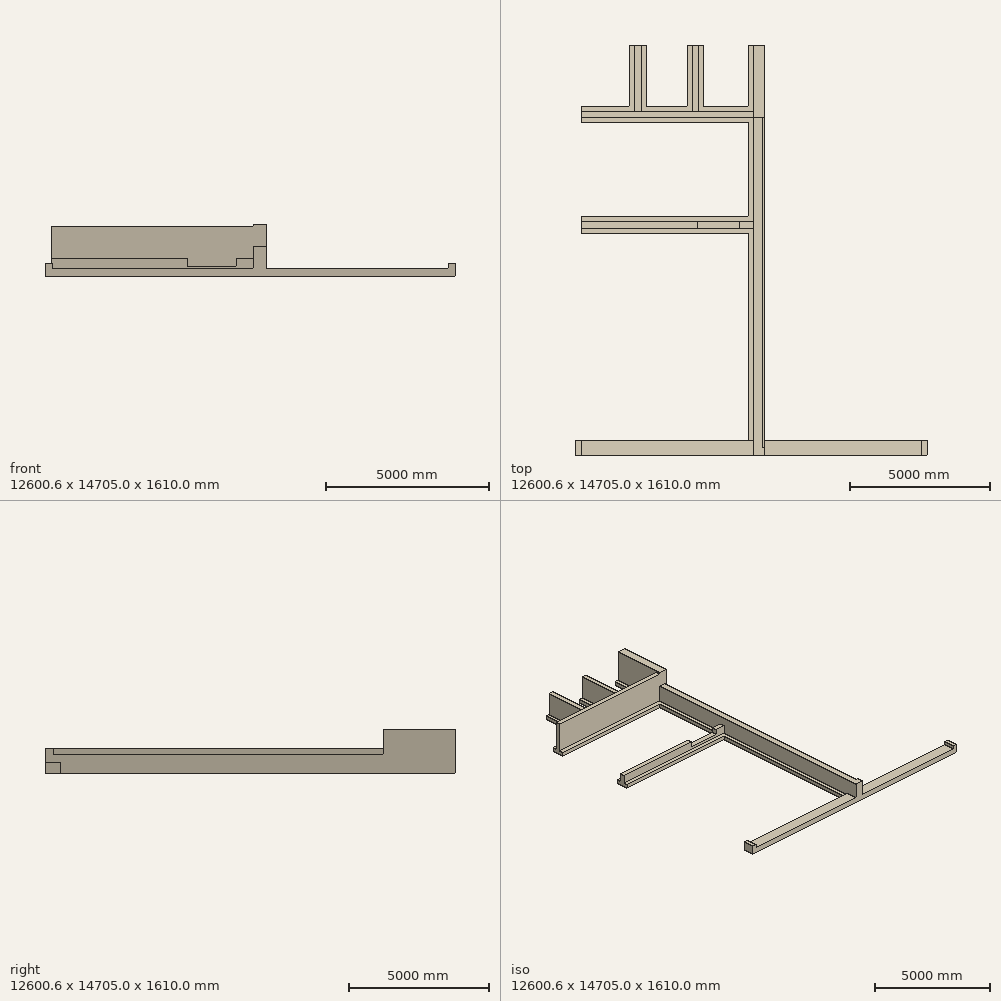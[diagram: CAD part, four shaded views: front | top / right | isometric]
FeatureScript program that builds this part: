
annotation { "Feature Type Name" : "Feature", "Feature Type Description" : "" }
export const myFeature = defineFeature(function(context is Context, id is Id, definition is map)
    precondition{}
    {
        {
            var Q0;
            Q0=qCreatedBy(makeId("Top.planeOp"),FACE);
            var sketch = newSketch(context, id + "F0", { "sketchPlane" : qUnion([Q0])});
            skLineSegment(sketch, "E0.bottom", {"start": v(0, 0) * mm, "end": v(590, 0) * mm});
            skLineSegment(sketch, "E0.top", {"start": v(0, 14705) * mm, "end": v(590, 14705) * mm});
            skLineSegment(sketch, "E0.left", {"start": v(0, 0) * mm, "end": v(0, 14705) * mm});
            skLineSegment(sketch, "E0.right", {"start": v(590, 0) * mm, "end": v(590, 14705) * mm});
            skLineSegment(sketch, "E1.bottom", {"start": v(0, 11945) * mm, "end": v(-5990, 11945) * mm});
            skLineSegment(sketch, "E1.top", {"start": v(0, 12535) * mm, "end": v(-5990, 12535) * mm});
            skLineSegment(sketch, "E1.right", {"start": v(-5990, 11945) * mm, "end": v(-5990, 12535) * mm});
            skLineSegment(sketch, "E2.bottom", {"start": v(0, 7965) * mm, "end": v(-5990, 7965) * mm});
            skLineSegment(sketch, "E2.top", {"start": v(0, 8555) * mm, "end": v(-5990, 8555) * mm});
            skLineSegment(sketch, "E2.right", {"start": v(-5990, 7965) * mm, "end": v(-5990, 8555) * mm});
            skLineSegment(sketch, "E3.bottom", {"start": v(-4250, 14705) * mm, "end": v(-3660, 14705) * mm});
            skLineSegment(sketch, "E3.left", {"start": v(-4250, 14705) * mm, "end": v(-4250, 12535) * mm});
            skLineSegment(sketch, "E3.right", {"start": v(-3660, 14705) * mm, "end": v(-3660, 12535) * mm});
            skLineSegment(sketch, "E4.top", {"start": v(-2200, 14705) * mm, "end": v(-1610, 14705) * mm});
            skLineSegment(sketch, "E4.left", {"start": v(-2200, 12535) * mm, "end": v(-2200, 14705) * mm});
            skLineSegment(sketch, "E4.right", {"start": v(-1610, 12535) * mm, "end": v(-1610, 14705) * mm});
            skSolve(sketch);
        }
        {
            var Q0;
            {var subQ3=sQuery(id+"F0.wireOp",EDGE,"E0.bottom");Q0=makeQuery(id+"F0.imprint","IMPRINT",FACE,{"disambiguationData":[TD([[makeQuery(id+"F0.imprint","IMPRINT",EDGE,{"derivedFrom":subQ3}),1.0]])]});}
            var Q1;
            Q1=makeQuery(id+"F0.imprint","IMPRINT",FACE,{"disambiguationData":[TD([[makeQuery(id+"F0.imprint","IMPRINT",EDGE,{"derivedFrom":sQuery(id+"F0.wireOp",EDGE,"E2.bottom")}),-1.0]])]});
            var Q2;
            Q2=makeQuery(id+"F0.imprint","IMPRINT",FACE,{"disambiguationData":[TD([[makeQuery(id+"F0.imprint","IMPRINT",EDGE,{"derivedFrom":sQuery(id+"F0.wireOp",EDGE,"E1.bottom")}),-1.0]])]});
            var Q3;
            Q3=makeQuery(id+"F0.imprint","IMPRINT",FACE,{"disambiguationData":[TD([[makeQuery(id+"F0.imprint","IMPRINT",EDGE,{"derivedFrom":sQuery(id+"F0.wireOp",EDGE,"E3.bottom")}),-1.0]])]});
            var Q4;
            Q4=makeQuery(id+"F0.imprint","IMPRINT",FACE,{"disambiguationData":[TD([[makeQuery(id+"F0.imprint","IMPRINT",EDGE,{"derivedFrom":sQuery(id+"F0.wireOp",EDGE,"yrg7KJtE-bSgN-jth9-biQU-cp0C4ELDEyeg.bottom")}),1.0]])]});
            var Q5;
            Q5=makeQuery(id+"F0.imprint","IMPRINT",FACE,{"disambiguationData":[TD([[makeQuery(id+"F0.imprint","IMPRINT",EDGE,{"derivedFrom":sQuery(id+"F0.wireOp",EDGE,"E4.top")}),-1.0]])]});
            extrude(context, id + "F1", {"entities" : qUnion([Q0, Q1, Q2, Q3, Q4, Q5]), "depth" : 180 * mm});
        }
        {
            var Q0;
            Q0=makeQuery(id+"F1.opExtrude","CAP_FACE",FACE,{"disambiguationData":[OSD([sQuery(id+"F0.wireOp",EDGE,"E0.bottom"),sQuery(id+"F0.wireOp",EDGE,"E0.top"),sQuery(id+"F0.wireOp",EDGE,"E0.left"),sQuery(id+"F0.wireOp",EDGE,"E0.right"),sQuery(id+"F0.wireOp",EDGE,"E1.bottom"),sQuery(id+"F0.wireOp",EDGE,"E1.top"),sQuery(id+"F0.wireOp",EDGE,"E1.right"),sQuery(id+"F0.wireOp",EDGE,"E2.bottom"),sQuery(id+"F0.wireOp",EDGE,"E2.top"),sQuery(id+"F0.wireOp",EDGE,"E2.right"),sQuery(id+"F0.wireOp",EDGE,"E3.bottom"),sQuery(id+"F0.wireOp",EDGE,"E3.left"),sQuery(id+"F0.wireOp",EDGE,"E3.right")])],"isStart":false});
            var sketch = newSketch(context, id + "F2", { "sketchPlane" : qUnion([Q0])});
            skLineSegment(sketch, "E5.bottom", {"start": v(590, 0) * mm, "end": v(195, 0) * mm});
            skLineSegment(sketch, "E5.top", {"start": v(590, 14705) * mm, "end": v(195, 14705) * mm});
            skLineSegment(sketch, "E5.left", {"start": v(590, 0) * mm, "end": v(590, 14705) * mm});
            skLineSegment(sketch, "E5.right", {"start": v(195, 0) * mm, "end": v(195, 14705) * mm});
            skSolve(sketch);
        }
        {
            var Q0;
            Q0 = qSketchRegion(id + "F2", true);
            extrude(context, id + "F3", {"entities" : qUnion([Q0]), "operationType" : NewBodyOperationType.ADD, "depth" : 750 * mm});
        }
        {
            var Q0;
            Q0=makeQuery(id+"F3.opExtrude","CAP_FACE",FACE,{"disambiguationData":[OSD([sQuery(id+"F2.wireOp",EDGE,"E5.bottom"),sQuery(id+"F2.wireOp",EDGE,"E5.top"),sQuery(id+"F2.wireOp",EDGE,"E5.left"),sQuery(id+"F2.wireOp",EDGE,"E5.right")])],"isStart":false});
            var sketch = newSketch(context, id + "F4", { "sketchPlane" : qUnion([Q0])});
            skLineSegment(sketch, "E6.bottom", {"start": v(590, 14705) * mm, "end": v(195, 14705) * mm});
            skLineSegment(sketch, "E6.top", {"start": v(590, 12135) * mm, "end": v(195, 12135) * mm});
            skLineSegment(sketch, "E6.left", {"start": v(590, 14705) * mm, "end": v(590, 12135) * mm});
            skLineSegment(sketch, "E6.right", {"start": v(195, 14705) * mm, "end": v(195, 12135) * mm});
            skSolve(sketch);
        }
        {
            var Q0;
            Q0 = qSketchRegion(id + "F4", true);
            extrude(context, id + "F5", {"entities" : qUnion([Q0]), "operationType" : NewBodyOperationType.ADD, "depth" : 680 * mm});
        }
        {
            var Q0;
            Q0=makeQuery(id+"F3.opExtrude","CAP_FACE",FACE,{"disambiguationData":[OSD([sQuery(id+"F2.wireOp",EDGE,"E5.bottom"),sQuery(id+"F2.wireOp",EDGE,"E5.top"),sQuery(id+"F2.wireOp",EDGE,"E5.left"),sQuery(id+"F2.wireOp",EDGE,"E5.right")])],"isStart":false});
            var sketch = newSketch(context, id + "F6", { "sketchPlane" : qUnion([Q0])});
            skLineSegment(sketch, "E7.bottom", {"start": v(590, 12135) * mm, "end": v(505, 12135) * mm});
            skLineSegment(sketch, "E7.top", {"start": v(590, 290) * mm, "end": v(505, 290) * mm});
            skLineSegment(sketch, "E7.left", {"start": v(590, 12135) * mm, "end": v(590, 290) * mm});
            skLineSegment(sketch, "E7.right", {"start": v(505, 12135) * mm, "end": v(505, 290) * mm});
            skSolve(sketch);
        }
        {
            var Q0;
            Q0 = qSketchRegion(id + "F6", true);
            extrude(context, id + "F7", {"entities" : qUnion([Q0]), "operationType" : NewBodyOperationType.REMOVE, "oppositeDirection" : true, "depth" : 220 * mm});
        }
        {
            var Q0;
            Q0=makeQuery(id+"F1.opExtrude","CAP_FACE",FACE,{"disambiguationData":[OSD([sQuery(id+"F0.wireOp",EDGE,"E0.bottom"),sQuery(id+"F0.wireOp",EDGE,"E0.top"),sQuery(id+"F0.wireOp",EDGE,"E0.left"),sQuery(id+"F0.wireOp",EDGE,"E0.right"),sQuery(id+"F0.wireOp",EDGE,"E1.bottom"),sQuery(id+"F0.wireOp",EDGE,"E1.top"),sQuery(id+"F0.wireOp",EDGE,"E1.right"),sQuery(id+"F0.wireOp",EDGE,"E2.bottom"),sQuery(id+"F0.wireOp",EDGE,"E2.top"),sQuery(id+"F0.wireOp",EDGE,"E2.right"),sQuery(id+"F0.wireOp",EDGE,"E3.bottom"),sQuery(id+"F0.wireOp",EDGE,"E3.left"),sQuery(id+"F0.wireOp",EDGE,"E3.right")])],"isStart":false});
            var sketch = newSketch(context, id + "F8", { "sketchPlane" : qUnion([Q0])});
            skLineSegment(sketch, "E8.bottom", {"start": v(-5990, 8375) * mm, "end": v(195, 8375) * mm});
            skLineSegment(sketch, "E8.top", {"start": v(-5990, 8145) * mm, "end": v(195, 8145) * mm});
            skLineSegment(sketch, "E8.left", {"start": v(-5990, 8375) * mm, "end": v(-5990, 8145) * mm});
            skLineSegment(sketch, "E8.right", {"start": v(195, 8375) * mm, "end": v(195, 8145) * mm});
            skSolve(sketch);
        }
        {
            var Q0;
            Q0 = qSketchRegion(id + "F8", true);
            extrude(context, id + "F9", {"entities" : qUnion([Q0]), "operationType" : NewBodyOperationType.ADD, "depth" : 380 * mm});
        }
        {
            var Q0;
            Q0=makeQuery(id+"F9.opExtrude","CAP_FACE",FACE,{"disambiguationData":[OSD([sQuery(id+"F8.wireOp",EDGE,"E8.bottom"),sQuery(id+"F8.wireOp",EDGE,"E8.top"),sQuery(id+"F8.wireOp",EDGE,"E8.left"),sQuery(id+"F8.wireOp",EDGE,"E8.right")])],"isStart":false});
            var sketch = newSketch(context, id + "F10", { "sketchPlane" : qUnion([Q0])});
            skLineSegment(sketch, "E9.bottom", {"start": v(-1835, 8375) * mm, "end": v(-305, 8375) * mm});
            skLineSegment(sketch, "E9.top", {"start": v(-1835, 8145) * mm, "end": v(-305, 8145) * mm});
            skLineSegment(sketch, "E9.left", {"start": v(-1835, 8375) * mm, "end": v(-1835, 8145) * mm});
            skLineSegment(sketch, "E9.right", {"start": v(-305, 8375) * mm, "end": v(-305, 8145) * mm});
            skSolve(sketch);
        }
        {
            var Q0;
            Q0 = qSketchRegion(id + "F10", true);
            extrude(context, id + "F11", {"entities" : qUnion([Q0]), "operationType" : NewBodyOperationType.REMOVE, "oppositeDirection" : true, "depth" : 235 * mm});
        }
        {
            var Q0;
            {var subQ0=sQuery(id+"F0.wireOp",EDGE,"E2.right");var subQ1=sQuery(id+"F0.wireOp",EDGE,"E1.right");var subQ2=sQuery(id+"F0.wireOp",EDGE,"E1.top");var subQ3=sQuery(id+"F0.wireOp",EDGE,"E3.left");var subQ4=sQuery(id+"F0.wireOp",EDGE,"E3.right");var subQ5=sQuery(id+"F0.wireOp",EDGE,"E4.left");var subQ6=sQuery(id+"F0.wireOp",EDGE,"E0.left");var subQ8=sQuery(id+"F0.wireOp",EDGE,"E4.right");var subQ9=sQuery(id+"F0.wireOp",EDGE,"E2.top");var subQ10=sQuery(id+"F0.wireOp",EDGE,"E0.top");var subQ11=sQuery(id+"F0.wireOp",EDGE,"E1.bottom");var subQ12=sQuery(id+"F0.wireOp",EDGE,"E3.bottom");var subQ13=sQuery(id+"F0.wireOp",EDGE,"E4.top");Q0=makeQuery(id+"F9.boolean.opBoolean","SPLIT",FACE,{"disambiguationData":[TD([makeQuery(id+"F1.opExtrude","SWEPT_FACE",FACE,{"disambiguationData":[OSD([subQ10])]})])],"derivedFrom":makeQuery(id+"F1.opExtrude","CAP_FACE",FACE,{"disambiguationData":[OSD([sQuery(id+"F0.wireOp",EDGE,"E0.bottom"),subQ10,subQ6,sQuery(id+"F0.wireOp",EDGE,"E0.right"),subQ11,subQ2,subQ1,sQuery(id+"F0.wireOp",EDGE,"E2.bottom"),subQ9,subQ0,subQ12,subQ3,subQ4,subQ13,subQ5,subQ8])],"isStart":false})});}
            var sketch = newSketch(context, id + "F12", { "sketchPlane" : qUnion([Q0])});
            skLineSegment(sketch, "E10.bottom", {"start": v(-5990, 12345) * mm, "end": v(195, 12345) * mm});
            skLineSegment(sketch, "E10.top", {"start": v(-5990, 12135) * mm, "end": v(195, 12135) * mm});
            skLineSegment(sketch, "E10.left", {"start": v(-5990, 12345) * mm, "end": v(-5990, 12135) * mm});
            skLineSegment(sketch, "E10.right", {"start": v(195, 12345) * mm, "end": v(195, 12135) * mm});
            skSolve(sketch);
        }
        {
            var Q0;
            Q0 = qSketchRegion(id + "F12", true);
            extrude(context, id + "F13", {"entities" : qUnion([Q0]), "operationType" : NewBodyOperationType.ADD, "depth" : 1060 * mm});
        }
        {
            var Q0;
            {var subQ0=sQuery(id+"F0.wireOp",EDGE,"E4.top");var subQ2=sQuery(id+"F0.wireOp",EDGE,"E3.right");var subQ4=sQuery(id+"F0.wireOp",EDGE,"E3.bottom");var subQ6=sQuery(id+"F0.wireOp",EDGE,"E1.right");var subQ8=sQuery(id+"F0.wireOp",EDGE,"E1.top");var subQ9=sQuery(id+"F0.wireOp",EDGE,"E3.left");var subQ11=sQuery(id+"F0.wireOp",EDGE,"E0.top");var subQ12=makeQuery(id+"F1.opExtrude","SWEPT_FACE",FACE,{"disambiguationData":[OSD([subQ11])]});var subQ15=sQuery(id+"F0.wireOp",EDGE,"E0.left");var subQ18=sQuery(id+"F0.wireOp",EDGE,"E4.right");var subQ21=sQuery(id+"F0.wireOp",EDGE,"E4.left");var subQ27=sQuery(id+"F0.wireOp",EDGE,"E2.right");var subQ28=sQuery(id+"F0.wireOp",EDGE,"E2.top");var subQ29=sQuery(id+"F0.wireOp",EDGE,"E1.bottom");Q0=makeQuery(id+"F13.boolean.opBoolean","SPLIT",FACE,{"disambiguationData":[TD([subQ12])],"derivedFrom":makeQuery(id+"F9.boolean.opBoolean","SPLIT",FACE,{"disambiguationData":[TD([subQ12])],"derivedFrom":makeQuery(id+"F1.opExtrude","CAP_FACE",FACE,{"disambiguationData":[OSD([sQuery(id+"F0.wireOp",EDGE,"E0.bottom"),subQ11,subQ15,sQuery(id+"F0.wireOp",EDGE,"E0.right"),subQ29,subQ8,subQ6,sQuery(id+"F0.wireOp",EDGE,"E2.bottom"),subQ28,subQ27,subQ4,subQ9,subQ2,subQ0,subQ21,subQ18])],"isStart":false})})});}
            var sketch = newSketch(context, id + "F14", { "sketchPlane" : qUnion([Q0])});
            skLineSegment(sketch, "E11.bottom", {"start": v(-4072.5, 14705) * mm, "end": v(-3837.5, 14705) * mm});
            skLineSegment(sketch, "E11.top", {"start": v(-4072.5, 12345) * mm, "end": v(-3837.5, 12345) * mm});
            skLineSegment(sketch, "E11.left", {"start": v(-4072.5, 14705) * mm, "end": v(-4072.5, 12345) * mm});
            skLineSegment(sketch, "E11.right", {"start": v(-3837.5, 14705) * mm, "end": v(-3837.5, 12345) * mm});
            skLineSegment(sketch, "E12.bottom", {"start": v(-2022.5, 14705) * mm, "end": v(-1787.5, 14705) * mm});
            skLineSegment(sketch, "E12.top", {"start": v(-2022.5, 12345) * mm, "end": v(-1787.5, 12345) * mm});
            skLineSegment(sketch, "E12.left", {"start": v(-2022.5, 14705) * mm, "end": v(-2022.5, 12345) * mm});
            skLineSegment(sketch, "E12.right", {"start": v(-1787.5, 14705) * mm, "end": v(-1787.5, 12345) * mm});
            skSolve(sketch);
        }
        {
            var Q0;
            Q0 = qSketchRegion(id + "F14", true);
            var Q1;
            Q1=makeQuery(id+"F13.opExtrude","CAP_FACE",FACE,{"disambiguationData":[OSD([sQuery(id+"F12.wireOp",EDGE,"E10.bottom"),sQuery(id+"F12.wireOp",EDGE,"E10.top"),sQuery(id+"F12.wireOp",EDGE,"E10.left"),sQuery(id+"F12.wireOp",EDGE,"E10.right")])],"isStart":false});
            extrude(context, id + "F15", {"entities" : qUnion([Q0]), "operationType" : NewBodyOperationType.ADD, "endBound" : BoundingType.UP_TO_SURFACE, "endBoundEntityFace" : qUnion([Q1]), "depth" : 25 * mm});
        }
        {
            var Q0;
            Q0=makeQuery(id+"F1.opExtrude","CAP_FACE",FACE,{"disambiguationData":[OSD([sQuery(id+"F0.wireOp",EDGE,"E0.bottom"),sQuery(id+"F0.wireOp",EDGE,"E0.top"),sQuery(id+"F0.wireOp",EDGE,"E0.left"),sQuery(id+"F0.wireOp",EDGE,"E0.right"),sQuery(id+"F0.wireOp",EDGE,"E1.bottom"),sQuery(id+"F0.wireOp",EDGE,"E1.top"),sQuery(id+"F0.wireOp",EDGE,"E1.right"),sQuery(id+"F0.wireOp",EDGE,"E2.bottom"),sQuery(id+"F0.wireOp",EDGE,"E2.top"),sQuery(id+"F0.wireOp",EDGE,"E2.right"),sQuery(id+"F0.wireOp",EDGE,"E3.bottom"),sQuery(id+"F0.wireOp",EDGE,"E3.left"),sQuery(id+"F0.wireOp",EDGE,"E3.right"),sQuery(id+"F0.wireOp",EDGE,"E4.top"),sQuery(id+"F0.wireOp",EDGE,"E4.left"),sQuery(id+"F0.wireOp",EDGE,"E4.right")])],"isStart":true});
            var sketch = newSketch(context, id + "F16", { "sketchPlane" : qUnion([Q0])});
            skLineSegment(sketch, "E13.bottom", {"start": v(-5990, -530) * mm, "end": v(6210, -530) * mm});
            skLineSegment(sketch, "E13.top", {"start": v(-5990, 0) * mm, "end": v(6210, 0) * mm});
            skLineSegment(sketch, "E13.left", {"start": v(-5990, -530) * mm, "end": v(-5990, 0) * mm});
            skLineSegment(sketch, "E13.right", {"start": v(6210, -530) * mm, "end": v(6210, 0) * mm});
            skSolve(sketch);
        }
        {
            var Q0;
            Q0 = qSketchRegion(id + "F16", true);
            extrude(context, id + "F17", {"entities" : qUnion([Q0]), "operationType" : NewBodyOperationType.ADD, "oppositeDirection" : true, "depth" : (75 + 180) * mm});
        }
        {
            var Q0;
            Q0=makeQuery(id+"F13.boolean.opBoolean","MERGE",FACE,{"derivedFrom":[makeQuery(id+"F7.boolean.opBoolean","MERGE",FACE,{"derivedFrom":[makeQuery(id+"F5.opExtrude","SWEPT_FACE",FACE,{"disambiguationData":[OSD([sQuery(id+"F4.wireOp",EDGE,"E6.top")])]}),makeQuery(id+"F7.opExtrude","SWEPT_FACE",FACE,{"disambiguationData":[OSD([sQuery(id+"F6.wireOp",EDGE,"E7.bottom")])]})]}),makeQuery(id+"F13.opExtrude","SWEPT_FACE",FACE,{"disambiguationData":[OSD([sQuery(id+"F12.wireOp",EDGE,"E10.top")])]})]});
            var sketch = newSketch(context, id + "F18", { "sketchPlane" : qUnion([Q0])});
            skLineSegment(sketch, "E14.bottom", {"start": v(505, 710) * mm, "end": v(590, 710) * mm});
            skLineSegment(sketch, "E14.top", {"start": v(505, 1610) * mm, "end": v(590, 1610) * mm});
            skLineSegment(sketch, "E14.left", {"start": v(505, 710) * mm, "end": v(505, 1610) * mm});
            skLineSegment(sketch, "E14.right", {"start": v(590, 710) * mm, "end": v(590, 1610) * mm});
            skSolve(sketch);
        }
        {
            var Q0;
            Q0 = qSketchRegion(id + "F18", true);
            extrude(context, id + "F19", {"entities" : qUnion([Q0]), "operationType" : NewBodyOperationType.REMOVE, "endBound" : BoundingType.THROUGH_ALL, "oppositeDirection" : true, "depth" : 25 * mm});
        }
        {
            var Q0;
            {var subQ0=sQuery(id+"F12.wireOp",EDGE,"E10.right");var subQ1=sQuery(id+"F12.wireOp",EDGE,"E10.left");var subQ2=sQuery(id+"F12.wireOp",EDGE,"E10.top");var subQ3=sQuery(id+"F12.wireOp",EDGE,"E10.bottom");Q0=makeQuery(id+"F15.boolean.opBoolean","MERGE",FACE,{"derivedFrom":[makeQuery(id+"F13.opExtrude","CAP_FACE",FACE,{"disambiguationData":[OSD([subQ3,subQ2,subQ1,subQ0])],"isStart":false}),makeQuery(id+"F15.opExtrude","CAP_FACE",FACE,{"disambiguationData":[OSD([subQ3,subQ2,subQ1,subQ0]),ownerDisambiguation([makeQuery(id+"F15.opExtrude","SWEPT_BODY",BODY,{"disambiguationData":[OSD([sQuery(id+"F14.wireOp",EDGE,"E11.bottom"),sQuery(id+"F14.wireOp",EDGE,"E11.top"),sQuery(id+"F14.wireOp",EDGE,"E11.left"),sQuery(id+"F14.wireOp",EDGE,"E11.right")])]})])],"isStart":false}),makeQuery(id+"F15.opExtrude","CAP_FACE",FACE,{"disambiguationData":[OSD([subQ3,subQ2,subQ1,subQ0]),ownerDisambiguation([makeQuery(id+"F15.opExtrude","SWEPT_BODY",BODY,{"disambiguationData":[OSD([sQuery(id+"F14.wireOp",EDGE,"E12.bottom"),sQuery(id+"F14.wireOp",EDGE,"E12.top"),sQuery(id+"F14.wireOp",EDGE,"E12.left"),sQuery(id+"F14.wireOp",EDGE,"E12.right")])]})])],"isStart":false})]});}
            var sketch = newSketch(context, id + "F20", { "sketchPlane" : qUnion([Q0])});
            skLineSegment(sketch, "E15.bottom", {"start": v(-5990, 12135) * mm, "end": v(195, 12135) * mm});
            skLineSegment(sketch, "E15.top", {"start": v(-5990, 12345) * mm, "end": v(195, 12345) * mm});
            skLineSegment(sketch, "E15.left", {"start": v(-5990, 12135) * mm, "end": v(-5990, 12345) * mm});
            skLineSegment(sketch, "E15.right", {"start": v(195, 12135) * mm, "end": v(195, 12345) * mm});
            skSolve(sketch);
        }
        {
            var Q0;
            Q0 = qSketchRegion(id + "F20", true);
            extrude(context, id + "F21", {"entities" : qUnion([Q0]), "operationType" : NewBodyOperationType.ADD, "depth" : 300 * mm});
        }
        {
            var Q0;
            Q0=makeQuery(id+"F19.boolean.opBoolean","MERGE",FACE,{"derivedFrom":[makeQuery(id+"F7.boolean.opBoolean","COPY",FACE,{"derivedFrom":makeQuery(id+"F7.opExtrude","CAP_FACE",FACE,{"disambiguationData":[OSD([sQuery(id+"F6.wireOp",EDGE,"E7.bottom"),sQuery(id+"F6.wireOp",EDGE,"E7.top"),sQuery(id+"F6.wireOp",EDGE,"E7.left"),sQuery(id+"F6.wireOp",EDGE,"E7.right")])],"isStart":false})}),makeQuery(id+"F19.opExtrude","SWEPT_FACE",FACE,{"disambiguationData":[OSD([sQuery(id+"F18.wireOp",EDGE,"E14.bottom")])]})]});
            var sketch = newSketch(context, id + "F22", { "sketchPlane" : qUnion([Q0])});
            skLineSegment(sketch, "E16.bottom", {"start": v(505, 14705) * mm, "end": v(590, 14705) * mm});
            skLineSegment(sketch, "E16.top", {"start": v(505, 12135) * mm, "end": v(590, 12135) * mm});
            skLineSegment(sketch, "E16.left", {"start": v(505, 14705) * mm, "end": v(505, 12135) * mm});
            skLineSegment(sketch, "E16.right", {"start": v(590, 14705) * mm, "end": v(590, 12135) * mm});
            skSolve(sketch);
        }
        {
            var Q0;
            Q0 = qSketchRegion(id + "F22", true);
            var Q1;
            Q1=makeQuery(id+"F5.opExtrude","CAP_FACE",FACE,{"disambiguationData":[OSD([sQuery(id+"F4.wireOp",EDGE,"E6.bottom"),sQuery(id+"F4.wireOp",EDGE,"E6.top"),sQuery(id+"F4.wireOp",EDGE,"E6.left"),sQuery(id+"F4.wireOp",EDGE,"E6.right")])],"isStart":false});
            extrude(context, id + "F23", {"entities" : qUnion([Q0]), "operationType" : NewBodyOperationType.ADD, "endBound" : BoundingType.UP_TO_SURFACE, "endBoundEntityFace" : qUnion([Q1]), "depth" : 25 * mm});
        }
        {
            var Q0;
            {var subQ0=sQuery(id+"F16.wireOp",EDGE,"E13.bottom");var subQ1=sQuery(id+"F16.wireOp",EDGE,"E13.top");var subQ2=sQuery(id+"F16.wireOp",EDGE,"E13.left");Q0=makeQuery(id+"F17.boolean.opBoolean","SPLIT",FACE,{"disambiguationData":[TD([makeQuery(id+"F3.opExtrude","SWEPT_FACE",FACE,{"disambiguationData":[OSD([sQuery(id+"F2.wireOp",EDGE,"E5.right")])]})])],"derivedFrom":makeQuery(id+"F17.opExtrude","CAP_FACE",FACE,{"disambiguationData":[OSD([subQ0,subQ1,subQ2,sQuery(id+"F16.wireOp",EDGE,"E13.right")])],"isStart":false})});}
            var sketch = newSketch(context, id + "F24", { "sketchPlane" : qUnion([Q0])});
            skLineSegment(sketch, "E17.bottom", {"start": v(-5990, 530) * mm, "end": v(-6190.1, 530) * mm});
            skLineSegment(sketch, "E17.top", {"start": v(-5990, 0) * mm, "end": v(-6190.1, 0) * mm});
            skLineSegment(sketch, "E17.left", {"start": v(-5990, 530) * mm, "end": v(-5990, 0) * mm});
            skLineSegment(sketch, "E17.right", {"start": v(-6190.1, 530) * mm, "end": v(-6190.1, 0) * mm});
            skSolve(sketch);
        }
        {
            var Q0;
            Q0=makeQuery(id+"F24.imprint","IMPRINT",FACE,{"disambiguationData":[TD([[makeQuery(id+"F24.imprint","IMPRINT",EDGE,{"derivedFrom":sQuery(id+"F24.wireOp",EDGE,"E17.bottom")}),1.0]])]});
            var Q1;
            Q1=makeQuery(id+"F17.boolean.opBoolean","MERGE",FACE,{"derivedFrom":[makeQuery(id+"F1.opExtrude","CAP_FACE",FACE,{"disambiguationData":[OSD([sQuery(id+"F0.wireOp",EDGE,"E0.bottom"),sQuery(id+"F0.wireOp",EDGE,"E0.top"),sQuery(id+"F0.wireOp",EDGE,"E0.left"),sQuery(id+"F0.wireOp",EDGE,"E0.right"),sQuery(id+"F0.wireOp",EDGE,"E1.bottom"),sQuery(id+"F0.wireOp",EDGE,"E1.top"),sQuery(id+"F0.wireOp",EDGE,"E1.right"),sQuery(id+"F0.wireOp",EDGE,"E2.bottom"),sQuery(id+"F0.wireOp",EDGE,"E2.top"),sQuery(id+"F0.wireOp",EDGE,"E2.right"),sQuery(id+"F0.wireOp",EDGE,"E3.bottom"),sQuery(id+"F0.wireOp",EDGE,"E3.left"),sQuery(id+"F0.wireOp",EDGE,"E3.right"),sQuery(id+"F0.wireOp",EDGE,"E4.top"),sQuery(id+"F0.wireOp",EDGE,"E4.left"),sQuery(id+"F0.wireOp",EDGE,"E4.right")])],"isStart":true}),makeQuery(id+"F17.opExtrude","CAP_FACE",FACE,{"disambiguationData":[OSD([sQuery(id+"F16.wireOp",EDGE,"E13.bottom"),sQuery(id+"F16.wireOp",EDGE,"E13.top"),sQuery(id+"F16.wireOp",EDGE,"E13.left"),sQuery(id+"F16.wireOp",EDGE,"E13.right")])],"isStart":true})]});
            extrude(context, id + "F25", {"entities" : qUnion([Q0]), "operationType" : NewBodyOperationType.ADD, "depth" : 145.1 * mm, "hasSecondDirection" : true, "secondDirectionBound" : SecondDirectionBoundingType.UP_TO_SURFACE, "secondDirectionOppositeDirection" : true, "secondDirectionBoundEntityFace" : qUnion([Q1]), "secondDirectionDepth" : 200 * mm});
        }
        {
            var Q0;
            {var subQ0=sQuery(id+"F16.wireOp",EDGE,"E13.right");var subQ1=sQuery(id+"F16.wireOp",EDGE,"E13.bottom");var subQ2=sQuery(id+"F16.wireOp",EDGE,"E13.top");Q0=makeQuery(id+"F17.boolean.opBoolean","SPLIT",FACE,{"disambiguationData":[TD([makeQuery(id+"F1.opExtrude","SWEPT_FACE",FACE,{"disambiguationData":[OSD([sQuery(id+"F0.wireOp",EDGE,"E0.right")])]})])],"derivedFrom":makeQuery(id+"F17.opExtrude","CAP_FACE",FACE,{"disambiguationData":[OSD([subQ1,subQ2,sQuery(id+"F16.wireOp",EDGE,"E13.left"),subQ0])],"isStart":false})});}
            var sketch = newSketch(context, id + "F26", { "sketchPlane" : qUnion([Q0])});
            skLineSegment(sketch, "E18.bottom", {"start": v(6210, 0) * mm, "end": v(6410.5, 0) * mm});
            skLineSegment(sketch, "E18.top", {"start": v(6210, 530) * mm, "end": v(6410.5, 530) * mm});
            skLineSegment(sketch, "E18.left", {"start": v(6210, 0) * mm, "end": v(6210, 530) * mm});
            skLineSegment(sketch, "E18.right", {"start": v(6410.5, 0) * mm, "end": v(6410.5, 530) * mm});
            skSolve(sketch);
        }
        {
            var Q0;
            Q0 = qSketchRegion(id + "F26", true);
            var Q1;
            {var subQ0=sQuery(id+"F16.wireOp",EDGE,"E13.right");var subQ1=sQuery(id+"F16.wireOp",EDGE,"E13.left");var subQ2=sQuery(id+"F16.wireOp",EDGE,"E13.top");var subQ3=sQuery(id+"F16.wireOp",EDGE,"E13.bottom");var subQ4=sQuery(id+"F0.wireOp",EDGE,"E4.right");var subQ5=sQuery(id+"F0.wireOp",EDGE,"E4.left");var subQ6=sQuery(id+"F0.wireOp",EDGE,"E4.top");var subQ7=sQuery(id+"F0.wireOp",EDGE,"E3.right");var subQ8=sQuery(id+"F0.wireOp",EDGE,"E3.left");var subQ9=sQuery(id+"F0.wireOp",EDGE,"E3.bottom");var subQ10=sQuery(id+"F0.wireOp",EDGE,"E2.right");var subQ11=sQuery(id+"F0.wireOp",EDGE,"E2.top");var subQ12=sQuery(id+"F0.wireOp",EDGE,"E2.bottom");var subQ13=sQuery(id+"F0.wireOp",EDGE,"E1.right");var subQ14=sQuery(id+"F0.wireOp",EDGE,"E1.top");var subQ15=sQuery(id+"F0.wireOp",EDGE,"E1.bottom");var subQ16=sQuery(id+"F0.wireOp",EDGE,"E0.right");var subQ17=sQuery(id+"F0.wireOp",EDGE,"E0.left");var subQ18=sQuery(id+"F0.wireOp",EDGE,"E0.top");var subQ19=sQuery(id+"F0.wireOp",EDGE,"E0.bottom");Q1=makeQuery(id+"F25.boolean.opBoolean","MERGE",FACE,{"derivedFrom":[makeQuery(id+"F17.boolean.opBoolean","MERGE",FACE,{"derivedFrom":[makeQuery(id+"F1.opExtrude","CAP_FACE",FACE,{"disambiguationData":[OSD([subQ19,subQ18,subQ17,subQ16,subQ15,subQ14,subQ13,subQ12,subQ11,subQ10,subQ9,subQ8,subQ7,subQ6,subQ5,subQ4])],"isStart":true}),makeQuery(id+"F17.opExtrude","CAP_FACE",FACE,{"disambiguationData":[OSD([subQ3,subQ2,subQ1,subQ0])],"isStart":true})]}),makeQuery(id+"F25.opExtrude","CAP_FACE",FACE,{"disambiguationData":[OSD([subQ19,subQ18,subQ17,subQ16,subQ15,subQ14,subQ13,subQ12,subQ11,subQ10,subQ9,subQ8,subQ7,subQ6,subQ5,subQ4,subQ3,subQ2,subQ1,subQ0])],"isStart":true})]});}
            extrude(context, id + "F27", {"entities" : qUnion([Q0]), "operationType" : NewBodyOperationType.ADD, "depth" : 145.5 * mm, "hasSecondDirection" : true, "secondDirectionBound" : SecondDirectionBoundingType.UP_TO_SURFACE, "secondDirectionOppositeDirection" : true, "secondDirectionBoundEntityFace" : qUnion([Q1]), "secondDirectionDepth" : 25 * mm});
        }
    });
